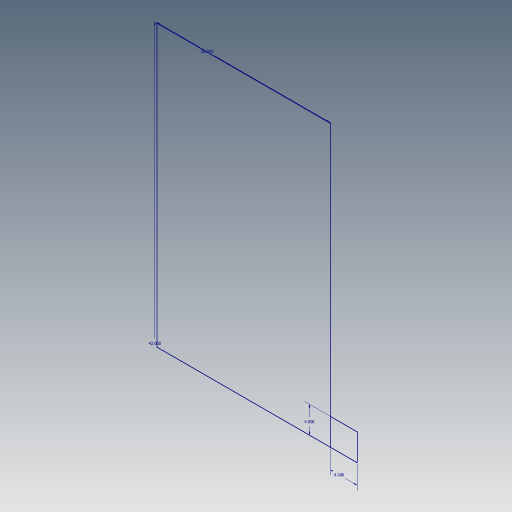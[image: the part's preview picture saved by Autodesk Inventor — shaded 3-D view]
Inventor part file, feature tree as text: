
AUTODESK INVENTOR PART (.ipt)
format: ipt  version: 2023.5 (Build 275446000, 446)  size: 78,336 bytes
history: native  units: in
note: dims shown in document units (in); Inventor stores cm internally (conversion verified against a paired STEP export)
features: sketch x1
ambient origin geometry x8: Origin, YZ Plane, XZ Plane, XY Plane, X Axis, Y Axis, Z Axis, Center Point
feature tree (1):
  sketch  "Sketch1"  dims[d0=26.0in d1=42.0in d2=4.0in d3=4.0in]
